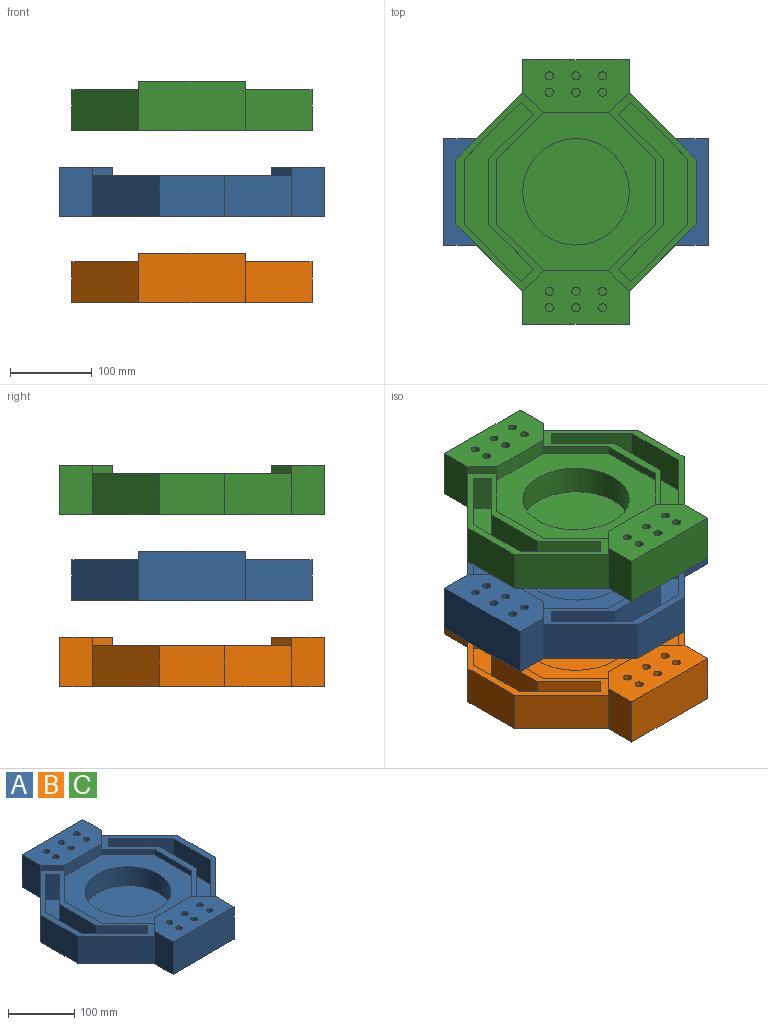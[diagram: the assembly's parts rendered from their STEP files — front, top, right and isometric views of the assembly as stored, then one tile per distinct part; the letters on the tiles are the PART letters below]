
ASSEMBLY  parts=3 mates=2
PART A: 74 faces, bbox 293.1x323.1x60 mm
  f0: plane 80x45mm, normal (-1,0,0), area 3600mm2, adj f36,f37,f43,f64
  f1: cylinder r=65mm len=130mm, axis (0,0,-1), area 14294.2mm2, adj f2,f59
  f2: plane 193.14x193.14mm, normal (0,0,1), area 17628.7mm2, adj f1,f15,f18,f30,f31,f32,f44,f45
  f3: plane 323.14x293.14mm, normal (0,0,-1), area 68365.6mm2, adj f5,f6,f7,f20,f21,f27,f33,f34
  f4: plane 25x25mm, normal (0.71,-0.71,0), area 353.6mm2, adj f5,f15,f16,f43
  f5: plane 60x40mm, normal (1,0,0), area 2400mm2, adj f3,f4,f6,f16,f42
  f6: plane 130x60mm, normal (0,1,0), area 7800mm2, adj f3,f5,f7,f16
  f7: plane 60x40mm, normal (-1,0,0), area 2400mm2, adj f3,f6,f8,f16,f46
  f8: plane 25x25mm, normal (-0.71,-0.71,0), area 353.6mm2, adj f7,f15,f16,f58
  f9: cylinder r=5mm len=55mm, axis (0,0,-1), area 1727.9mm2, adj f16,f63
  f10: cylinder r=5mm len=55mm, axis (0,0,-1), area 1727.9mm2, adj f16,f62
  f11: cylinder r=5mm len=55mm, axis (0,0,-1), area 1727.9mm2, adj f16,f69
  f12: cylinder r=5mm len=55mm, axis (0,0,-1), area 1727.9mm2, adj f16,f70
  f13: cylinder r=5mm len=55mm, axis (0,0,-1), area 1727.9mm2, adj f16,f61
  f14: cylinder r=5mm len=55mm, axis (0,0,-1), area 1727.9mm2, adj f16,f60
  f15: plane 80x20mm, normal (0,-1,0), area 1600mm2, adj f2,f4,f8,f16,f30,f44
  f16: plane 130x65mm, normal (0,0,1), area 7353.8mm2, adj f4,f5,f6,f7,f8,f9,f10,f11
  f17: plane 25x25mm, normal (0.71,0.71,0), area 353.6mm2, adj f18,f27,f29,f43
  f18: plane 80x20mm, normal (0,1,0), area 1600mm2, adj f2,f17,f19,f29,f31,f45
  f19: plane 25x25mm, normal (-0.71,0.71,0), area 353.6mm2, adj f18,f20,f29,f58
  f20: plane 60x40mm, normal (-1,0,0), area 2400mm2, adj f3,f19,f21,f29,f48
  f21: plane 130x60mm, normal (0,-1,0), area 7800mm2, adj f3,f20,f27,f29
  f22: cylinder r=5mm len=55mm, axis (0,0,-1), area 1727.9mm2, adj f29,f66
  f23: cylinder r=5mm len=55mm, axis (0,0,-1), area 1727.9mm2, adj f29,f67
  f24: cylinder r=5mm len=55mm, axis (0,0,-1), area 1727.9mm2, adj f29,f73
  f25: cylinder r=5mm len=55mm, axis (0,0,-1), area 1727.9mm2, adj f29,f72
  f26: cylinder r=5mm len=55mm, axis (0,0,-1), area 1727.9mm2, adj f29,f68
  f27: plane 60x40mm, normal (1,0,0), area 2400mm2, adj f3,f17,f21,f29,f33
  f28: cylinder r=5mm len=55mm, axis (0,0,-1), area 1727.9mm2, adj f29,f65
  f29: plane 130x65mm, normal (0,0,1), area 7353.8mm2, adj f17,f18,f19,f20,f21,f22,f23,f24
  f30: plane 56.57x56.57mm, normal (-0.71,-0.71,0), area 800mm2, adj f2,f15,f32,f43
  f31: plane 56.57x56.57mm, normal (-0.71,0.71,0), area 800mm2, adj f2,f18,f32,f43
  f32: plane 80x10mm, normal (-1,0,0), area 800mm2, adj f2,f30,f31,f43
  f33: plane 81.57x81.57mm, normal (0.71,-0.71,0), area 5767.8mm2, adj f3,f27,f34,f43
  f34: plane 80x50mm, normal (1,0,0), area 4000mm2, adj f3,f33,f42,f43
  f35: plane 45x15mm, normal (0.71,-0.71,0), area 954.6mm2, adj f36,f41,f43,f64
  f36: plane 69.5x69.5mm, normal (-0.71,-0.71,0), area 4422.8mm2, adj f0,f35,f43,f64
  f37: plane 69.5x69.5mm, normal (-0.71,0.71,0), area 4422.8mm2, adj f0,f38,f43,f64
  f38: plane 45x15mm, normal (0.71,0.71,0), area 954.6mm2, adj f37,f39,f43,f64
  f39: plane 54.5x54.5mm, normal (0.71,-0.71,0), area 3468.2mm2, adj f38,f40,f43,f64
  f40: plane 80x45mm, normal (1,0,0), area 3600mm2, adj f39,f41,f43,f64
  f41: plane 54.5x54.5mm, normal (0.71,0.71,0), area 3468.2mm2, adj f35,f40,f43,f64
  f42: plane 81.57x81.57mm, normal (0.71,0.71,0), area 5767.8mm2, adj f3,f5,f34,f43
  f43: plane 243.14x106.57mm, normal (0,0,1), area 4787mm2, adj f0,f4,f17,f30,f31,f32,f33,f34
  f44: plane 56.57x56.57mm, normal (0.71,-0.71,0), area 800mm2, adj f2,f15,f57,f58
  f45: plane 56.57x56.57mm, normal (0.71,0.71,0), area 800mm2, adj f2,f18,f57,f58
  f46: plane 81.57x81.57mm, normal (-0.71,0.71,0), area 5767.8mm2, adj f3,f7,f47,f58
  f47: plane 80x50mm, normal (-1,0,0), area 4000mm2, adj f3,f46,f48,f58
  f48: plane 81.57x81.57mm, normal (-0.71,-0.71,0), area 5767.8mm2, adj f3,f20,f47,f58
  f49: plane 80x45mm, normal (1,0,0), area 3600mm2, adj f50,f56,f58,f71
  f50: plane 69.5x69.5mm, normal (0.71,-0.71,0), area 4422.8mm2, adj f49,f51,f58,f71
  f51: plane 45x15mm, normal (-0.71,-0.71,0), area 954.6mm2, adj f50,f52,f58,f71
  f52: plane 54.5x54.5mm, normal (-0.71,0.71,0), area 3468.2mm2, adj f51,f53,f58,f71
  f53: plane 80x45mm, normal (-1,0,0), area 3600mm2, adj f52,f54,f58,f71
  f54: plane 54.5x54.5mm, normal (-0.71,-0.71,0), area 3468.2mm2, adj f53,f55,f58,f71
  f55: plane 45x15mm, normal (-0.71,0.71,0), area 954.6mm2, adj f54,f56,f58,f71
  f56: plane 69.5x69.5mm, normal (0.71,0.71,0), area 4422.8mm2, adj f49,f55,f58,f71
  f57: plane 80x10mm, normal (1,0,0), area 800mm2, adj f2,f44,f45,f58
  f58: plane 243.14x106.57mm, normal (0,0,1), area 4787mm2, adj f8,f19,f44,f45,f46,f47,f48,f49
  f59: plane 130x130mm, normal (0,0,1), area 13273.2mm2, adj f1
  f60: plane 10x10mm, normal (0,0,1), area 78.5mm2, adj f14
  f61: plane 10x10mm, normal (0,0,1), area 78.5mm2, adj f13
  f62: plane 10x10mm, normal (0,0,1), area 78.5mm2, adj f10
  f63: plane 10x10mm, normal (0,0,1), area 78.5mm2, adj f9
  f64: plane 219x84.5mm, normal (0,0,1), area 6119.8mm2, adj f0,f35,f36,f37,f38,f39,f40,f41
  f65: plane 10x10mm, normal (0,0,1), area 78.5mm2, adj f28
  f66: plane 10x10mm, normal (0,0,1), area 78.5mm2, adj f22
  f67: plane 10x10mm, normal (0,0,1), area 78.5mm2, adj f23
  f68: plane 10x10mm, normal (0,0,1), area 78.5mm2, adj f26
  f69: plane 10x10mm, normal (0,0,1), area 78.5mm2, adj f11
  f70: plane 10x10mm, normal (0,0,1), area 78.5mm2, adj f12
  f71: plane 219x84.5mm, normal (0,0,1), area 6119.8mm2, adj f49,f50,f51,f52,f53,f54,f55,f56
  f72: plane 10x10mm, normal (0,0,1), area 78.5mm2, adj f25
  f73: plane 10x10mm, normal (0,0,1), area 78.5mm2, adj f24
PART B: same geometry as A
PART C: same geometry as A
PLACE A rot(axis=(0,0,-1),90deg) t=(-51.49,0,102.48)mm
PLACE B t=(-51.49,0,-2.52)mm
PLACE C rot(axis=(0,0,1),0deg) t=(-51.49,0,207.48)mm
MATE fastened C.f1 <-> A.f1  axis (0,0,-1) through (-51.49,0,207.48)mm
MATE fastened A.f1 <-> B.f1  axis (0,0,-1) through (-51.49,0,102.48)mm
